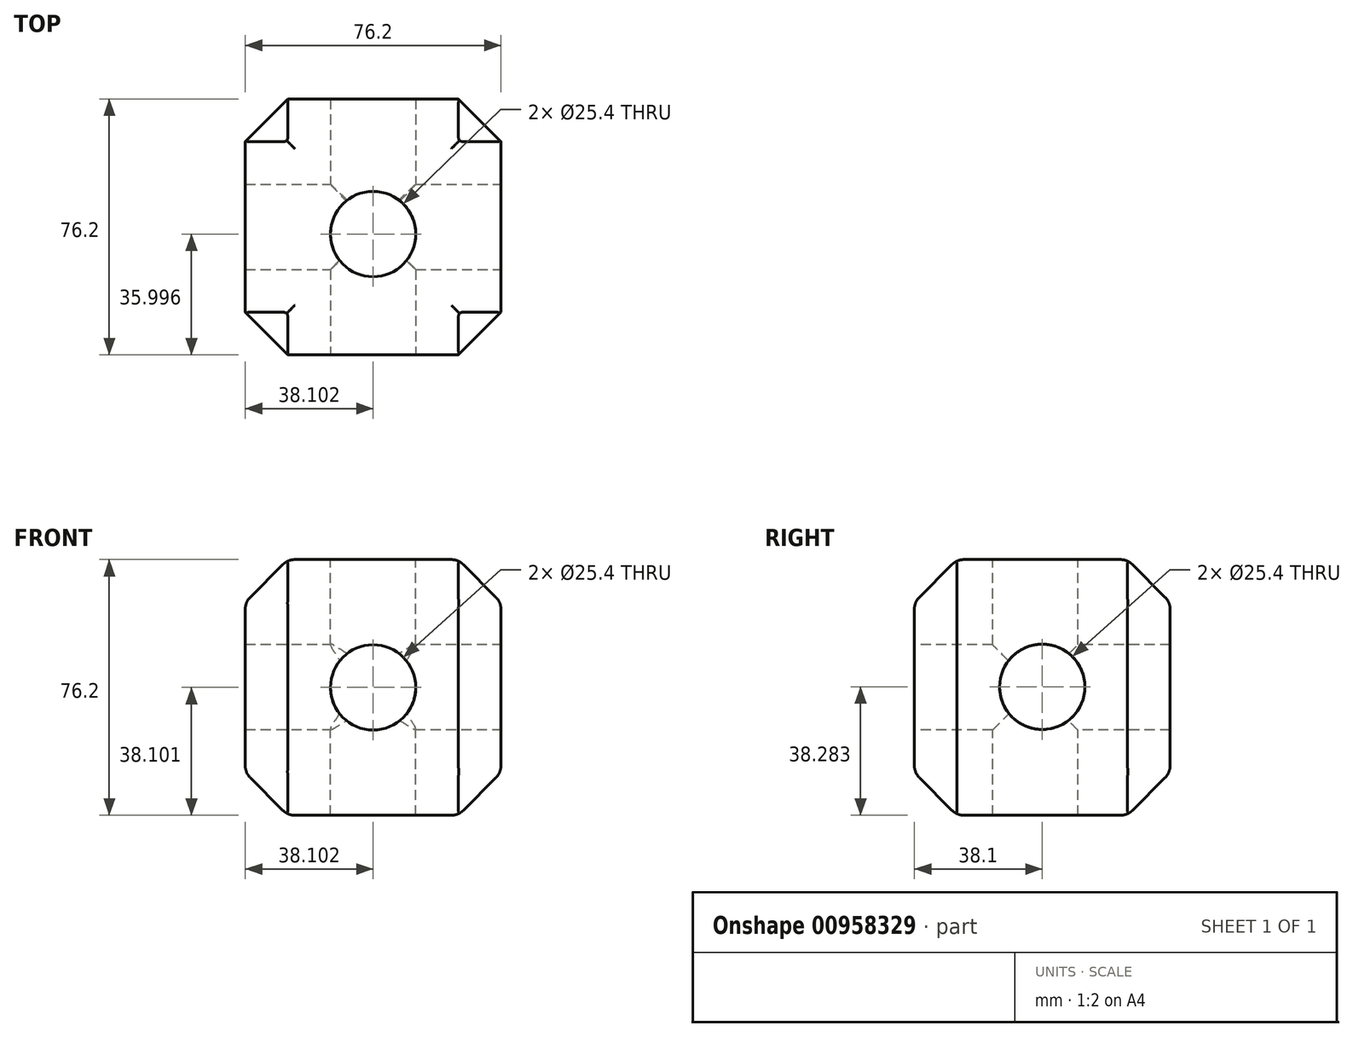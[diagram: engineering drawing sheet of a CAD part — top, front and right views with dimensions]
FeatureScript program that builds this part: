
annotation { "Feature Type Name" : "Feature", "Feature Type Description" : "" }
export const myFeature = defineFeature(function(context is Context, id is Id, definition is map)
    precondition{}
    {
        {
            var Q0;
            Q0=qCreatedBy(makeId("Front.planeOp"),FACE);
            var sketch = newSketch(context, id + "F0", { "sketchPlane" : qUnion([Q0])});
            skLineSegment(sketch, "E0.bottom", {"start": v(-92.64, 87.4) * mm, "end": v(-16.44, 87.4) * mm});
            skLineSegment(sketch, "E0.top", {"start": v(-92.64, 11.2) * mm, "end": v(-16.44, 11.2) * mm});
            skLineSegment(sketch, "E0.left", {"start": v(-92.64, 87.4) * mm, "end": v(-92.64, 11.2) * mm});
            skLineSegment(sketch, "E0.right", {"start": v(-16.44, 87.4) * mm, "end": v(-16.44, 11.2) * mm});
            skSolve(sketch);
        }
        {
            var Q0;
            Q0=makeQuery(id+"F0.imprint","IMPRINT",FACE,{"disambiguationData":[TD([[makeQuery(id+"F0.imprint","IMPRINT",EDGE,{"derivedFrom":sQuery(id+"F0.wireOp",EDGE,"E0.bottom")}),-1.0]])]});
            extrude(context, id + "F1", {"entities" : qUnion([Q0]), "depth" : 76.2 * mm, "offsetDistance" : 25.4 * mm});
        }
        {
            var Q0;
            Q0=makeQuery(id+"F1.opExtrude","CAP_EDGE",EDGE,{"disambiguationData":[OSD([sQuery(id+"F0.wireOp",EDGE,"E0.bottom")])],"isStart":false});
            var Q1;
            Q1=makeQuery(id+"F1.opExtrude","SWEPT_EDGE",EDGE,{"disambiguationData":[OSD([sQuery(id+"F0.wireOp",EDGE,"E0.bottom"),sQuery(id+"F0.wireOp",EDGE,"E0.left")])]});
            var Q2;
            Q2=makeQuery(id+"F1.opExtrude","CAP_EDGE",EDGE,{"disambiguationData":[OSD([sQuery(id+"F0.wireOp",EDGE,"E0.bottom")])],"isStart":true});
            var Q3;
            Q3=makeQuery(id+"F1.opExtrude","SWEPT_FACE",FACE,{"disambiguationData":[OSD([sQuery(id+"F0.wireOp",EDGE,"E0.bottom")])]});
            var Q4;
            Q4=makeQuery(id+"F1.opExtrude","CAP_EDGE",EDGE,{"disambiguationData":[OSD([sQuery(id+"F0.wireOp",EDGE,"E0.top")])],"isStart":false});
            var Q5;
            Q5=makeQuery(id+"F1.opExtrude","CAP_EDGE",EDGE,{"disambiguationData":[OSD([sQuery(id+"F0.wireOp",EDGE,"E0.right")])],"isStart":false});
            var Q6;
            Q6=makeQuery(id+"F1.opExtrude","SWEPT_EDGE",EDGE,{"disambiguationData":[OSD([sQuery(id+"F0.wireOp",EDGE,"E0.top"),sQuery(id+"F0.wireOp",EDGE,"E0.right")])]});
            var Q7;
            Q7=makeQuery(id+"F1.opExtrude","CAP_EDGE",EDGE,{"disambiguationData":[OSD([sQuery(id+"F0.wireOp",EDGE,"E0.top")])],"isStart":true});
            var Q8;
            Q8=makeQuery(id+"F1.opExtrude","SWEPT_EDGE",EDGE,{"disambiguationData":[OSD([sQuery(id+"F0.wireOp",EDGE,"E0.top"),sQuery(id+"F0.wireOp",EDGE,"E0.left")])]});
            var Q9;
            Q9=makeQuery(id+"F1.opExtrude","CAP_EDGE",EDGE,{"disambiguationData":[OSD([sQuery(id+"F0.wireOp",EDGE,"E0.left")])],"isStart":true});
            var Q10;
            Q10=makeQuery(id+"F1.opExtrude","CAP_EDGE",EDGE,{"disambiguationData":[OSD([sQuery(id+"F0.wireOp",EDGE,"E0.left")])],"isStart":false});
            var Q11;
            Q11=makeQuery(id+"F1.opExtrude","CAP_EDGE",EDGE,{"disambiguationData":[OSD([sQuery(id+"F0.wireOp",EDGE,"E0.right")])],"isStart":true});
            chamfer(context, id + "F2", {"entities" : qUnion([Q0, Q1, Q2, Q3, Q4, Q5, Q6, Q7, Q8, Q9, Q10, Q11]), "width" : 12.7 * mm, "tangentPropagation" : true});
        }
        {
            var Q0;
            {var subQ0=sQuery(id+"F0.wireOp",EDGE,"E0.bottom");Q0=makeQuery(id+"F2.opChamfer","BLEND_EDGE",EDGE,{"blendedFrom":[makeQuery(id+"F1.opExtrude","CAP_EDGE",EDGE,{"disambiguationData":[OSD([subQ0])],"isStart":false}),makeQuery(id+"F1.opExtrude","SWEPT_FACE",FACE,{"disambiguationData":[OSD([subQ0])]})],"blendedInto":[makeQuery(id+"F1.opExtrude","SWEPT_FACE",FACE,{"disambiguationData":[OSD([subQ0])]})]});}
            var Q1;
            {var subQ0=sQuery(id+"F0.wireOp",EDGE,"E0.bottom");Q1=makeQuery(id+"F2.opChamfer","BLEND_EDGE",EDGE,{"blendedFrom":[makeQuery(id+"F1.opExtrude","CAP_EDGE",EDGE,{"disambiguationData":[OSD([subQ0])],"isStart":false}),makeQuery(id+"F1.opExtrude","CAP_FACE",FACE,{"disambiguationData":[OSD([subQ0,sQuery(id+"F0.wireOp",EDGE,"E0.top"),sQuery(id+"F0.wireOp",EDGE,"E0.left"),sQuery(id+"F0.wireOp",EDGE,"E0.right")])],"isStart":false})],"blendedInto":[makeQuery(id+"F1.opExtrude","CAP_FACE",FACE,{"disambiguationData":[OSD([subQ0,sQuery(id+"F0.wireOp",EDGE,"E0.top"),sQuery(id+"F0.wireOp",EDGE,"E0.left"),sQuery(id+"F0.wireOp",EDGE,"E0.right")])],"isStart":false})]});}
            var Q2;
            {var subQ0=sQuery(id+"F0.wireOp",EDGE,"E0.right");Q2=makeQuery(id+"F2.opChamfer","BLEND_EDGE",EDGE,{"blendedFrom":[makeQuery(id+"F1.opExtrude","CAP_VERTEX",VERTEX,{"disambiguationData":[OSD([sQuery(id+"F0.wireOp",EDGE,"E0.bottom"),subQ0])],"isStart":false}),makeQuery(id+"F1.opExtrude","CAP_EDGE",EDGE,{"disambiguationData":[OSD([subQ0])],"isStart":false})],"blendedInto":[]});}
            var Q3;
            {var subQ0=sQuery(id+"F0.wireOp",EDGE,"E0.bottom");Q3=makeQuery(id+"F2.opChamfer","BLEND_EDGE",EDGE,{"blendedFrom":[makeQuery(id+"F1.opExtrude","SWEPT_EDGE",EDGE,{"disambiguationData":[OSD([subQ0,sQuery(id+"F0.wireOp",EDGE,"E0.right")])]}),makeQuery(id+"F1.opExtrude","SWEPT_FACE",FACE,{"disambiguationData":[OSD([subQ0])]})],"blendedInto":[makeQuery(id+"F1.opExtrude","SWEPT_FACE",FACE,{"disambiguationData":[OSD([subQ0])]})]});}
            var Q4;
            {var subQ0=sQuery(id+"F0.wireOp",EDGE,"E0.right");Q4=makeQuery(id+"F2.opChamfer","BLEND_EDGE",EDGE,{"blendedFrom":[makeQuery(id+"F1.opExtrude","SWEPT_EDGE",EDGE,{"disambiguationData":[OSD([sQuery(id+"F0.wireOp",EDGE,"E0.bottom"),subQ0])]}),makeQuery(id+"F1.opExtrude","SWEPT_FACE",FACE,{"disambiguationData":[OSD([subQ0])]})],"blendedInto":[makeQuery(id+"F1.opExtrude","SWEPT_FACE",FACE,{"disambiguationData":[OSD([subQ0])]})]});}
            var Q5;
            {var subQ0=sQuery(id+"F0.wireOp",EDGE,"E0.bottom");Q5=makeQuery(id+"F2.opChamfer","BLEND_EDGE",EDGE,{"blendedFrom":[makeQuery(id+"F1.opExtrude","SWEPT_EDGE",EDGE,{"disambiguationData":[OSD([subQ0,sQuery(id+"F0.wireOp",EDGE,"E0.left")])]}),makeQuery(id+"F1.opExtrude","SWEPT_FACE",FACE,{"disambiguationData":[OSD([subQ0])]})],"blendedInto":[makeQuery(id+"F1.opExtrude","SWEPT_FACE",FACE,{"disambiguationData":[OSD([subQ0])]})]});}
            var Q6;
            {var subQ0=sQuery(id+"F0.wireOp",EDGE,"E0.bottom");Q6=makeQuery(id+"F2.opChamfer","BLEND_EDGE",EDGE,{"blendedFrom":[makeQuery(id+"F1.opExtrude","CAP_EDGE",EDGE,{"disambiguationData":[OSD([subQ0])],"isStart":true}),makeQuery(id+"F1.opExtrude","SWEPT_FACE",FACE,{"disambiguationData":[OSD([subQ0])]})],"blendedInto":[makeQuery(id+"F1.opExtrude","SWEPT_FACE",FACE,{"disambiguationData":[OSD([subQ0])]})]});}
            var Q7;
            {var subQ0=sQuery(id+"F0.wireOp",EDGE,"E0.left");Q7=makeQuery(id+"F2.opChamfer","BLEND_EDGE",EDGE,{"blendedFrom":[makeQuery(id+"F1.opExtrude","SWEPT_EDGE",EDGE,{"disambiguationData":[OSD([sQuery(id+"F0.wireOp",EDGE,"E0.bottom"),subQ0])]}),makeQuery(id+"F1.opExtrude","SWEPT_FACE",FACE,{"disambiguationData":[OSD([subQ0])]})],"blendedInto":[makeQuery(id+"F1.opExtrude","SWEPT_FACE",FACE,{"disambiguationData":[OSD([subQ0])]})]});}
            var Q8;
            {var subQ0=sQuery(id+"F0.wireOp",EDGE,"E0.bottom");Q8=makeQuery(id+"F2.opChamfer","BLEND_EDGE",EDGE,{"blendedFrom":[makeQuery(id+"F1.opExtrude","CAP_EDGE",EDGE,{"disambiguationData":[OSD([subQ0])],"isStart":true}),makeQuery(id+"F1.opExtrude","CAP_FACE",FACE,{"disambiguationData":[OSD([subQ0,sQuery(id+"F0.wireOp",EDGE,"E0.top"),sQuery(id+"F0.wireOp",EDGE,"E0.left"),sQuery(id+"F0.wireOp",EDGE,"E0.right")])],"isStart":true})],"blendedInto":[makeQuery(id+"F1.opExtrude","CAP_FACE",FACE,{"disambiguationData":[OSD([subQ0,sQuery(id+"F0.wireOp",EDGE,"E0.top"),sQuery(id+"F0.wireOp",EDGE,"E0.left"),sQuery(id+"F0.wireOp",EDGE,"E0.right")])],"isStart":true})]});}
            var Q9;
            {var subQ0=sQuery(id+"F0.wireOp",EDGE,"E0.left");Q9=makeQuery(id+"F2.opChamfer","BLEND_EDGE",EDGE,{"blendedFrom":[makeQuery(id+"F1.opExtrude","CAP_VERTEX",VERTEX,{"disambiguationData":[OSD([sQuery(id+"F0.wireOp",EDGE,"E0.bottom"),subQ0])],"isStart":true}),makeQuery(id+"F1.opExtrude","CAP_EDGE",EDGE,{"disambiguationData":[OSD([subQ0])],"isStart":true})],"blendedInto":[]});}
            var Q10;
            {var subQ0=sQuery(id+"F0.wireOp",EDGE,"E0.right");Q10=makeQuery(id+"F2.opChamfer","BLEND_EDGE",EDGE,{"blendedFrom":[makeQuery(id+"F1.opExtrude","CAP_VERTEX",VERTEX,{"disambiguationData":[OSD([sQuery(id+"F0.wireOp",EDGE,"E0.bottom"),subQ0])],"isStart":true}),makeQuery(id+"F1.opExtrude","CAP_EDGE",EDGE,{"disambiguationData":[OSD([subQ0])],"isStart":true})],"blendedInto":[]});}
            var Q11;
            {var subQ0=sQuery(id+"F0.wireOp",EDGE,"E0.left");Q11=makeQuery(id+"F2.opChamfer","BLEND_EDGE",EDGE,{"blendedFrom":[makeQuery(id+"F1.opExtrude","CAP_VERTEX",VERTEX,{"disambiguationData":[OSD([sQuery(id+"F0.wireOp",EDGE,"E0.bottom"),subQ0])],"isStart":false}),makeQuery(id+"F1.opExtrude","CAP_EDGE",EDGE,{"disambiguationData":[OSD([subQ0])],"isStart":false})],"blendedInto":[]});}
            var Q12;
            {var subQ0=sQuery(id+"F0.wireOp",EDGE,"E0.right");Q12=makeQuery(id+"F2.opChamfer","BLEND_EDGE",EDGE,{"blendedFrom":[makeQuery(id+"F1.opExtrude","SWEPT_EDGE",EDGE,{"disambiguationData":[OSD([sQuery(id+"F0.wireOp",EDGE,"E0.top"),subQ0])]}),makeQuery(id+"F1.opExtrude","SWEPT_FACE",FACE,{"disambiguationData":[OSD([subQ0])]})],"blendedInto":[makeQuery(id+"F1.opExtrude","SWEPT_FACE",FACE,{"disambiguationData":[OSD([subQ0])]})]});}
            var Q13;
            {var subQ0=sQuery(id+"F0.wireOp",EDGE,"E0.top");Q13=makeQuery(id+"F2.opChamfer","BLEND_EDGE",EDGE,{"blendedFrom":[makeQuery(id+"F1.opExtrude","SWEPT_EDGE",EDGE,{"disambiguationData":[OSD([subQ0,sQuery(id+"F0.wireOp",EDGE,"E0.right")])]}),makeQuery(id+"F1.opExtrude","SWEPT_FACE",FACE,{"disambiguationData":[OSD([subQ0])]})],"blendedInto":[makeQuery(id+"F1.opExtrude","SWEPT_FACE",FACE,{"disambiguationData":[OSD([subQ0])]})]});}
            var Q14;
            {var subQ0=sQuery(id+"F0.wireOp",EDGE,"E0.right");Q14=makeQuery(id+"F2.opChamfer","BLEND_EDGE",EDGE,{"blendedFrom":[makeQuery(id+"F1.opExtrude","CAP_VERTEX",VERTEX,{"disambiguationData":[OSD([sQuery(id+"F0.wireOp",EDGE,"E0.top"),subQ0])],"isStart":false}),makeQuery(id+"F1.opExtrude","CAP_EDGE",EDGE,{"disambiguationData":[OSD([subQ0])],"isStart":false})],"blendedInto":[]});}
            var Q15;
            {var subQ0=sQuery(id+"F0.wireOp",EDGE,"E0.top");Q15=makeQuery(id+"F2.opChamfer","BLEND_EDGE",EDGE,{"blendedFrom":[makeQuery(id+"F1.opExtrude","CAP_EDGE",EDGE,{"disambiguationData":[OSD([subQ0])],"isStart":false}),makeQuery(id+"F1.opExtrude","CAP_FACE",FACE,{"disambiguationData":[OSD([sQuery(id+"F0.wireOp",EDGE,"E0.bottom"),subQ0,sQuery(id+"F0.wireOp",EDGE,"E0.left"),sQuery(id+"F0.wireOp",EDGE,"E0.right")])],"isStart":false})],"blendedInto":[makeQuery(id+"F1.opExtrude","CAP_FACE",FACE,{"disambiguationData":[OSD([sQuery(id+"F0.wireOp",EDGE,"E0.bottom"),subQ0,sQuery(id+"F0.wireOp",EDGE,"E0.left"),sQuery(id+"F0.wireOp",EDGE,"E0.right")])],"isStart":false})]});}
            var Q16;
            {var subQ0=sQuery(id+"F0.wireOp",EDGE,"E0.top");Q16=makeQuery(id+"F2.opChamfer","BLEND_EDGE",EDGE,{"blendedFrom":[makeQuery(id+"F1.opExtrude","CAP_EDGE",EDGE,{"disambiguationData":[OSD([subQ0])],"isStart":false}),makeQuery(id+"F1.opExtrude","SWEPT_FACE",FACE,{"disambiguationData":[OSD([subQ0])]})],"blendedInto":[makeQuery(id+"F1.opExtrude","SWEPT_FACE",FACE,{"disambiguationData":[OSD([subQ0])]})]});}
            var Q17;
            {var subQ0=sQuery(id+"F0.wireOp",EDGE,"E0.left");Q17=makeQuery(id+"F2.opChamfer","BLEND_EDGE",EDGE,{"blendedFrom":[makeQuery(id+"F1.opExtrude","CAP_VERTEX",VERTEX,{"disambiguationData":[OSD([sQuery(id+"F0.wireOp",EDGE,"E0.top"),subQ0])],"isStart":false}),makeQuery(id+"F1.opExtrude","CAP_EDGE",EDGE,{"disambiguationData":[OSD([subQ0])],"isStart":false})],"blendedInto":[]});}
            var Q18;
            {var subQ0=sQuery(id+"F0.wireOp",EDGE,"E0.left");Q18=makeQuery(id+"F2.opChamfer","BLEND_EDGE",EDGE,{"blendedFrom":[makeQuery(id+"F1.opExtrude","SWEPT_EDGE",EDGE,{"disambiguationData":[OSD([sQuery(id+"F0.wireOp",EDGE,"E0.top"),subQ0])]}),makeQuery(id+"F1.opExtrude","SWEPT_FACE",FACE,{"disambiguationData":[OSD([subQ0])]})],"blendedInto":[makeQuery(id+"F1.opExtrude","SWEPT_FACE",FACE,{"disambiguationData":[OSD([subQ0])]})]});}
            var Q19;
            {var subQ0=sQuery(id+"F0.wireOp",EDGE,"E0.top");Q19=makeQuery(id+"F2.opChamfer","BLEND_EDGE",EDGE,{"blendedFrom":[makeQuery(id+"F1.opExtrude","SWEPT_EDGE",EDGE,{"disambiguationData":[OSD([subQ0,sQuery(id+"F0.wireOp",EDGE,"E0.left")])]}),makeQuery(id+"F1.opExtrude","SWEPT_FACE",FACE,{"disambiguationData":[OSD([subQ0])]})],"blendedInto":[makeQuery(id+"F1.opExtrude","SWEPT_FACE",FACE,{"disambiguationData":[OSD([subQ0])]})]});}
            var Q20;
            {var subQ0=sQuery(id+"F0.wireOp",EDGE,"E0.left");Q20=makeQuery(id+"F2.opChamfer","BLEND_EDGE",EDGE,{"blendedFrom":[makeQuery(id+"F1.opExtrude","CAP_VERTEX",VERTEX,{"disambiguationData":[OSD([sQuery(id+"F0.wireOp",EDGE,"E0.top"),subQ0])],"isStart":true}),makeQuery(id+"F1.opExtrude","CAP_EDGE",EDGE,{"disambiguationData":[OSD([subQ0])],"isStart":true})],"blendedInto":[]});}
            var Q21;
            {var subQ0=sQuery(id+"F0.wireOp",EDGE,"E0.top");Q21=makeQuery(id+"F2.opChamfer","BLEND_EDGE",EDGE,{"blendedFrom":[makeQuery(id+"F1.opExtrude","CAP_EDGE",EDGE,{"disambiguationData":[OSD([subQ0])],"isStart":true}),makeQuery(id+"F1.opExtrude","CAP_FACE",FACE,{"disambiguationData":[OSD([sQuery(id+"F0.wireOp",EDGE,"E0.bottom"),subQ0,sQuery(id+"F0.wireOp",EDGE,"E0.left"),sQuery(id+"F0.wireOp",EDGE,"E0.right")])],"isStart":true})],"blendedInto":[makeQuery(id+"F1.opExtrude","CAP_FACE",FACE,{"disambiguationData":[OSD([sQuery(id+"F0.wireOp",EDGE,"E0.bottom"),subQ0,sQuery(id+"F0.wireOp",EDGE,"E0.left"),sQuery(id+"F0.wireOp",EDGE,"E0.right")])],"isStart":true})]});}
            var Q22;
            {var subQ0=sQuery(id+"F0.wireOp",EDGE,"E0.top");Q22=makeQuery(id+"F2.opChamfer","BLEND_EDGE",EDGE,{"blendedFrom":[makeQuery(id+"F1.opExtrude","CAP_EDGE",EDGE,{"disambiguationData":[OSD([subQ0])],"isStart":true}),makeQuery(id+"F1.opExtrude","SWEPT_FACE",FACE,{"disambiguationData":[OSD([subQ0])]})],"blendedInto":[makeQuery(id+"F1.opExtrude","SWEPT_FACE",FACE,{"disambiguationData":[OSD([subQ0])]})]});}
            var Q23;
            {var subQ0=sQuery(id+"F0.wireOp",EDGE,"E0.right");Q23=makeQuery(id+"F2.opChamfer","BLEND_EDGE",EDGE,{"blendedFrom":[makeQuery(id+"F1.opExtrude","CAP_VERTEX",VERTEX,{"disambiguationData":[OSD([sQuery(id+"F0.wireOp",EDGE,"E0.top"),subQ0])],"isStart":true}),makeQuery(id+"F1.opExtrude","CAP_EDGE",EDGE,{"disambiguationData":[OSD([subQ0])],"isStart":true})],"blendedInto":[]});}
            fillet(context, id + "F3", {"entities" : qUnion([Q0, Q1, Q2, Q3, Q4, Q5, Q6, Q7, Q8, Q9, Q10, Q11, Q12, Q13, Q14, Q15, Q16, Q17, Q18, Q19, Q20, Q21, Q22, Q23]), "radius" : 5.08 * mm, "tangentPropagation" : true, "allowEdgeOverflow" : false});
        }
        {
            var Q0;
            Q0=makeQuery(id+"F1.opExtrude","CAP_FACE",FACE,{"disambiguationData":[OSD([sQuery(id+"F0.wireOp",EDGE,"E0.bottom"),sQuery(id+"F0.wireOp",EDGE,"E0.top"),sQuery(id+"F0.wireOp",EDGE,"E0.left"),sQuery(id+"F0.wireOp",EDGE,"E0.right")])],"isStart":false});
            var sketch = newSketch(context, id + "F4", { "sketchPlane" : qUnion([Q0])});
            skCircle(sketch, "E1", {"center": v(-54.54, 49.3) * mm, "radius": 12.7 * mm});
            skPoint(sketch, "E1.centerSnap0", {"position": v(-79.94, 49.3) * mm});
            skSolve(sketch);
        }
        {
            var Q0;
            Q0=makeQuery(id+"F4.imprint","IMPRINT",FACE,{"disambiguationData":[TD([[makeQuery(id+"F4.imprint","IMPRINT",EDGE,{"derivedFrom":sQuery(id+"F4.wireOp",EDGE,"E1")}),1.0]])]});
            extrude(context, id + "F5", {"entities" : qUnion([Q0]), "operationType" : NewBodyOperationType.REMOVE, "endBound" : BoundingType.THROUGH_ALL, "oppositeDirection" : true, "depth" : 25.4 * mm, "offsetDistance" : 25.4 * mm});
        }
        {
            var Q0;
            Q0=makeQuery(id+"F1.opExtrude","SWEPT_FACE",FACE,{"disambiguationData":[OSD([sQuery(id+"F0.wireOp",EDGE,"E0.right")])]});
            var sketch = newSketch(context, id + "F6", { "sketchPlane" : qUnion([Q0])});
            skCircle(sketch, "E2", {"center": v(-38.1, 49.48) * mm, "radius": 12.7 * mm});
            skSolve(sketch);
        }
        {
            var Q0;
            Q0=makeQuery(id+"F6.imprint","IMPRINT",FACE,{"disambiguationData":[TD([[makeQuery(id+"F6.imprint","IMPRINT",EDGE,{"derivedFrom":sQuery(id+"F6.wireOp",EDGE,"E2")}),1.0]])]});
            extrude(context, id + "F7", {"entities" : qUnion([Q0]), "operationType" : NewBodyOperationType.REMOVE, "endBound" : BoundingType.THROUGH_ALL, "oppositeDirection" : true, "depth" : 25.4 * mm, "offsetDistance" : 25.4 * mm});
        }
        {
            var Q0;
            Q0=makeQuery(id+"F1.opExtrude","SWEPT_FACE",FACE,{"disambiguationData":[OSD([sQuery(id+"F0.wireOp",EDGE,"E0.bottom")])]});
            var sketch = newSketch(context, id + "F8", { "sketchPlane" : qUnion([Q0])});
            skCircle(sketch, "E3", {"center": v(-54.54, -40.2) * mm, "radius": 12.7 * mm});
            skPoint(sketch, "E3.centerSnap0", {"position": v(-54.54, -14.8) * mm});
            skSolve(sketch);
        }
        {
            var Q0;
            Q0=makeQuery(id+"F8.imprint","IMPRINT",FACE,{"disambiguationData":[TD([[makeQuery(id+"F8.imprint","IMPRINT",EDGE,{"derivedFrom":sQuery(id+"F8.wireOp",EDGE,"E3")}),1.0]])]});
            extrude(context, id + "F9", {"entities" : qUnion([Q0]), "operationType" : NewBodyOperationType.REMOVE, "endBound" : BoundingType.THROUGH_ALL, "oppositeDirection" : true, "depth" : 25.4 * mm, "offsetDistance" : 25.4 * mm});
        }
    });
